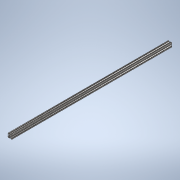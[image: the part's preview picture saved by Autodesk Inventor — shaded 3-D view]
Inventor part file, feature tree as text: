
AUTODESK INVENTOR PART (.ipt)
format: ipt  version: 2020 (Build 240168000, 168)  size: 246,784 bytes
history: native  units: in
note: dims shown in document units (in); Inventor stores cm internally (conversion verified against a paired STEP export)
features: extrude x1, sketch x1
ambient origin geometry x8: Origin, YZ Plane, XZ Plane, XY Plane, X Axis, Y Axis, Z Axis, Center Point
bodies: Solid1 (feature_tree)
feature tree (2):
  extrude  "Extrusion1"  [1 undecoded]
  sketch  "Sketch1"  dims[d0=39.0in d1=0.0in]
note: 1 required parameter value undecoded (feature->parameter linkage not recoverable at this tier; creation-order binding heuristic only, values carry confidence <= 0.55)
